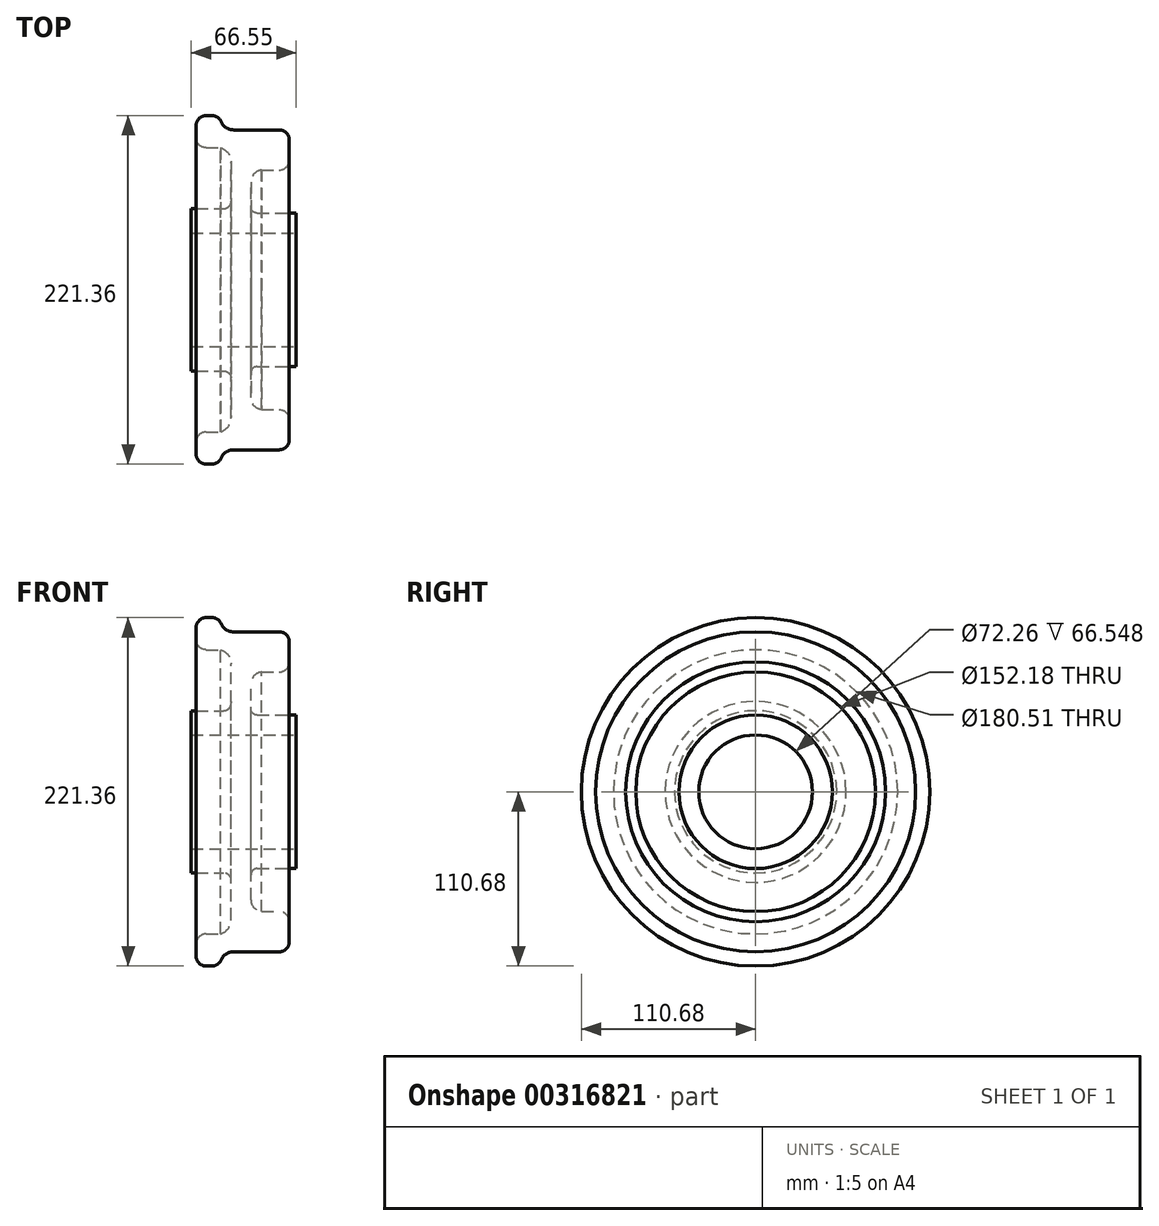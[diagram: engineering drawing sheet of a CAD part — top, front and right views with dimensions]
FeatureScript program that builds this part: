
annotation { "Feature Type Name" : "Feature", "Feature Type Description" : "" }
export const myFeature = defineFeature(function(context is Context, id is Id, definition is map)
    precondition{}
    {
        {
            var Q0;
            Q0=qCreatedBy(makeId("Front.planeOp"),FACE);
            var sketch = newSketch(context, id + "F0", { "sketchPlane" : qUnion([Q0])});
            skLineSegment(sketch, "E0", {"start": v(-41.25, 81.1) * mm, "end": v(-41.25, 57.45) * mm});
            skLineSegment(sketch, "E1", {"start": v(-28.7, 68.51) * mm, "end": v(-28.7, 52.7) * mm});
            skLineSegment(sketch, "E2", {"start": v(-63.46, 96.6) * mm, "end": v(-63.46, 104.33) * mm});
            skLineSegment(sketch, "E3", {"start": v(-57.11, 110.68) * mm, "end": v(-53.47, 110.68) * mm});
            skLineSegment(sketch, "E4", {"start": v(0, 48.75) * mm, "end": v(0, 36.13) * mm});
            skLineSegment(sketch, "E5", {"start": v(0, 36.13) * mm, "end": v(-66.55, 36.13) * mm});
            skArc(sketch, "E6", {"start": v(-47.63, 106.83) * mm, "mid": v(-44.45, 103.02) * mm, "end": v(-39.7, 101.6) * mm});
            skLineSegment(sketch, "E7", {"start": v(-10.64, 76.09) * mm, "end": v(-21.76, 76.09) * mm});
            skArc(sketch, "E8", {"start": v(-21.76, 76.09) * mm, "mid": v(-26.7, 73.65) * mm, "end": v(-28.7, 68.51) * mm});
            skLineSegment(sketch, "E9", {"start": v(-66.55, 36.13) * mm, "end": v(-66.55, 51.52) * mm});
            skLineSegment(sketch, "E10", {"start": v(-66.55, 51.52) * mm, "end": v(-46.1, 51.52) * mm});
            skLineSegment(sketch, "E11", {"start": v(0, 48.75) * mm, "end": v(-24.74, 48.75) * mm});
            skArc(sketch, "E12", {"start": v(-46.1, 51.52) * mm, "mid": v(-42.27, 53.34) * mm, "end": v(-41.25, 57.45) * mm});
            skArc(sketch, "E13", {"start": v(-28.7, 52.7) * mm, "mid": v(-27.53, 49.91) * mm, "end": v(-24.74, 48.75) * mm});
            skLineSegment(sketch, "E14", {"start": v(39.07, 0) * mm, "end": v(-96.59, 0) * mm, "construction": true});
            skLineSegment(sketch, "E15", {"start": v(-57.11, 90.26) * mm, "end": v(-48.05, 90.26) * mm});
            skArc(sketch, "E16", {"start": v(-41.25, 81.1) * mm, "mid": v(-43.14, 86.8) * mm, "end": v(-48.05, 90.26) * mm});
            skPoint(sketch, "E17.visualSharp", {"position": v(-63.46, 110.68) * mm});
            skArc(sketch, "E17.filletArc", {"start": v(-57.11, 110.68) * mm, "mid": v(-61.6, 108.82) * mm, "end": v(-63.46, 104.33) * mm});
            skPoint(sketch, "E18.visualSharp", {"position": v(-48.31, 110.68) * mm});
            skArc(sketch, "E18.filletArc", {"start": v(-47.63, 106.83) * mm, "mid": v(-49.97, 109.63) * mm, "end": v(-53.47, 110.68) * mm});
            skPoint(sketch, "E19.visualSharp", {"position": v(-63.46, 90.26) * mm});
            skArc(sketch, "E19.filletArc", {"start": v(-63.46, 96.6) * mm, "mid": v(-61.6, 92.12) * mm, "end": v(-57.11, 90.26) * mm});
            skArc(sketch, "E20.filletArc", {"start": v(-10.64, 76.09) * mm, "mid": v(-6.11, 77.98) * mm, "end": v(-4.3, 82.54) * mm});
            skLineSegment(sketch, "E21", {"start": v(-4.3, 82.54) * mm, "end": v(-4.3, 95.25) * mm});
            skLineSegment(sketch, "E22", {"start": v(-10.64, 101.6) * mm, "end": v(-39.7, 101.6) * mm});
            skPoint(sketch, "E23.visualSharp", {"position": v(-4.3, 101.6) * mm});
            skArc(sketch, "E23.filletArc", {"start": v(-4.3, 95.25) * mm, "mid": v(-6.15, 99.74) * mm, "end": v(-10.64, 101.6) * mm});
            skSolve(sketch);
        }
        {
            var Q0;
            Q0=makeQuery(id+"F0.imprint","IMPRINT",FACE,{"disambiguationData":[TD([[makeQuery(id+"F0.imprint","IMPRINT",EDGE,{"derivedFrom":sQuery(id+"F0.wireOp",EDGE,"E0")}),1.0]])]});
            var Q1;
            Q1=sQuery(id+"F0.wireOp",EDGE,"E14");
            revolve(context, id + "F1", {"entities" : qUnion([Q0]), "axis" : qUnion([Q1]), "revolveType" : RevolveType.FULL});
        }
    });
